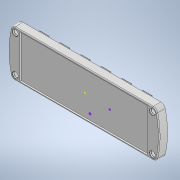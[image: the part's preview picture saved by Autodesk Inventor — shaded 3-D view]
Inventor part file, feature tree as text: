
AUTODESK INVENTOR PART (.ipt)
format: ipt  version: 2021 (Build 250183000, 183)  size: 685,568 bytes
history: native  units: mm
features: other x1, sketch x1
ambient origin geometry x8: Origin, YZ Plane, XZ Plane, XY Plane, X Axis, Y Axis, Z Axis, Center Point
bodies: Solid1 (feature_tree)
feature tree (2):
  other  "1009799_3D"
  sketch  "Sketch1"
